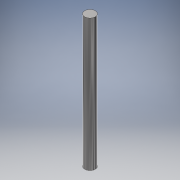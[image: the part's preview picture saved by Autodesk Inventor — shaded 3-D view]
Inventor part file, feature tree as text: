
AUTODESK INVENTOR PART (.ipt)
format: ipt  version: 2016 (Build 200138000, 138)  size: 89,600 bytes
history: native  units: mm
features: extrude x1, sketch x1
ambient origin geometry x8: Origin, YZ Plane, XZ Plane, XY Plane, X Axis, Y Axis, Z Axis, Center Point
bodies: Solid1 (feature_tree)
feature tree (2):
  extrude  "Extrusion1"  Depth=100.0mm TaperAngle=0.0deg
  sketch  "Sketch1"  dims[d0=8.0mm d1=100.0mm d2=0.0mm]
